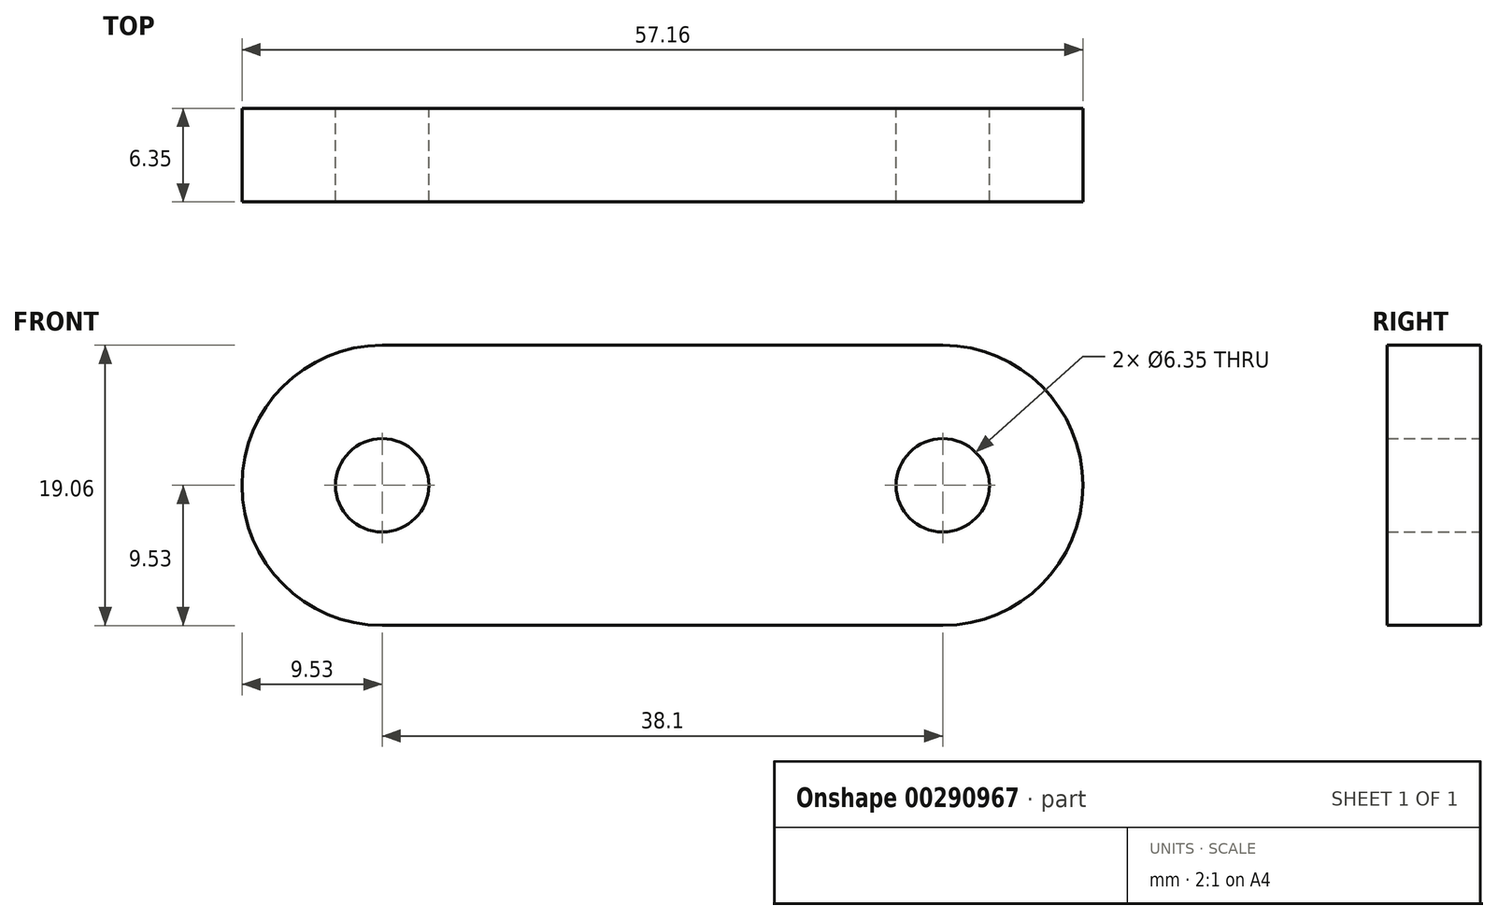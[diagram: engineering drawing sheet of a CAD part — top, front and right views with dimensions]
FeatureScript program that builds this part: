
annotation { "Feature Type Name" : "Feature", "Feature Type Description" : "" }
export const myFeature = defineFeature(function(context is Context, id is Id, definition is map)
    precondition{}
    {
        {
            var Q0;
            Q0=qCreatedBy(makeId("Front.planeOp"),FACE);
            var sketch = newSketch(context, id + "F0", { "sketchPlane" : qUnion([Q0])});
            skLineSegment(sketch, "E0.bottom", {"start": v(-19.05, -9.53) * mm, "end": v(19.05, -9.53) * mm});
            skLineSegment(sketch, "E0.top", {"start": v(-19.05, 9.53) * mm, "end": v(19.05, 9.53) * mm});
            skPoint(sketch, "E0.middle", {"position": v(0, 0) * mm});
            skCircle(sketch, "E1", {"center": v(-19.05, 0) * mm, "radius": 3.18 * mm});
            skCircle(sketch, "E2", {"center": v(19.05, 0) * mm, "radius": 3.18 * mm});
            skArc(sketch, "E3", {"start": v(-19.05, 9.53) * mm, "mid": v(-28.58, 0) * mm, "end": v(-19.05, -9.53) * mm});
            skArc(sketch, "E4", {"start": v(19.05, -9.53) * mm, "mid": v(28.58, 0) * mm, "end": v(19.05, 9.53) * mm});
            skSolve(sketch);
        }
        {
            var Q0;
            Q0=makeQuery(id+"F0.imprint","IMPRINT",FACE,{"disambiguationData":[TD([[makeQuery(id+"F0.imprint","IMPRINT",EDGE,{"derivedFrom":sQuery(id+"F0.wireOp",EDGE,"E0.bottom")}),1.0]])]});
            extrude(context, id + "F1", {"entities" : qUnion([Q0]), "depth" : 6.35 * mm});
        }
    });
